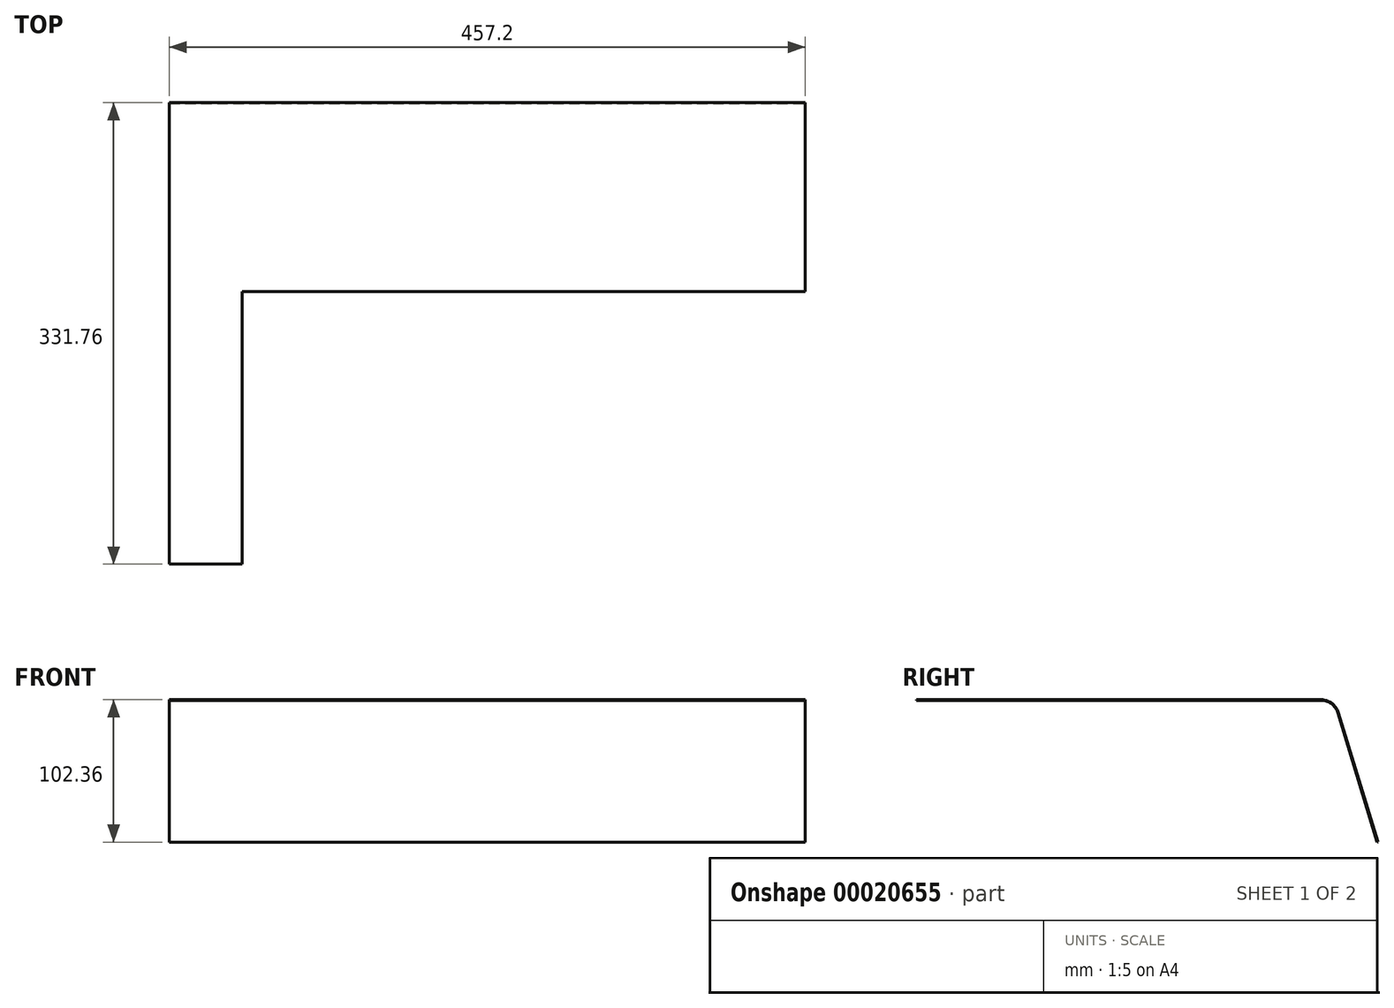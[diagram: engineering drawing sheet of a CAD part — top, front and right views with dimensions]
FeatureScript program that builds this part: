
annotation { "Feature Type Name" : "Feature", "Feature Type Description" : "" }
export const myFeature = defineFeature(function(context is Context, id is Id, definition is map)
    precondition{}
    {
        {
            var Q0;
            Q0=qCreatedBy(makeId("Right.planeOp"),FACE);
            var sketch = newSketch(context, id + "F0", { "sketchPlane" : qUnion([Q0])});
            skLineSegment(sketch, "E0", {"start": v(-259.13, 0) * mm, "end": v(31.98, 0) * mm});
            skLineSegment(sketch, "E1", {"start": v(44.12, -8.99) * mm, "end": v(72.63, -102.21) * mm});
            skPoint(sketch, "E2.visualSharp", {"position": v(41.38, 0) * mm});
            skArc(sketch, "E2.filletArc", {"start": v(44.12, -8.99) * mm, "mid": v(39.53, -2.5) * mm, "end": v(31.98, 0) * mm});
            skLineSegment(sketch, "E3.0", {"start": v(43.65, -9.13) * mm, "end": v(72.15, -102.36) * mm});
            skArc(sketch, "E3.1", {"start": v(43.65, -9.13) * mm, "mid": v(39.24, -2.9) * mm, "end": v(31.98, -0.5) * mm});
            skLineSegment(sketch, "E3.2", {"start": v(-259.13, -0.5) * mm, "end": v(31.98, -0.5) * mm});
            skLineSegment(sketch, "E4", {"start": v(-259.13, -0.5) * mm, "end": v(-259.13, 0) * mm});
            skLineSegment(sketch, "E5", {"start": v(72.15, -102.36) * mm, "end": v(72.63, -102.21) * mm});
            skSolve(sketch);
        }
        {
            var Q0;
            Q0=makeQuery(id+"F0.imprint","IMPRINT",FACE,{"disambiguationData":[TD([[makeQuery(id+"F0.imprint","IMPRINT",EDGE,{"derivedFrom":sQuery(id+"F0.wireOp",EDGE,"E0")}),-1.0]])]});
            extrude(context, id + "F1", {"entities" : qUnion([Q0]), "oppositeDirection" : true, "depth" : 457.2 * mm, "symmetric" : true});
        }
        {
            var Q0;
            Q0=qCreatedBy(makeId("Top.planeOp"),FACE);
            var sketch = newSketch(context, id + "F2", { "sketchPlane" : qUnion([Q0])});
            skCircle(sketch, "E6", {"center": v(-27.64, -26.13) * mm, "radius": 1.25 * mm});
            skCircle(sketch, "E7.0.1.0", {"center": v(-27.64, 26.13) * mm, "radius": 1.25 * mm});
            skCircle(sketch, "E7.1.0.0", {"center": v(27.64, -26.13) * mm, "radius": 1.25 * mm});
            skCircle(sketch, "E7.1.1.0", {"center": v(27.64, 26.13) * mm, "radius": 1.25 * mm});
            skSolve(sketch);
        }
        {
            var Q0;
            Q0=makeQuery(id+"F2.imprint","IMPRINT",FACE,{"disambiguationData":[TD([[makeQuery(id+"F2.imprint","IMPRINT",EDGE,{"derivedFrom":sQuery(id+"F2.wireOp",EDGE,"E7.0.1.0")}),1.0]])]});
            var Q1;
            Q1=makeQuery(id+"F2.imprint","IMPRINT",FACE,{"disambiguationData":[TD([[makeQuery(id+"F2.imprint","IMPRINT",EDGE,{"derivedFrom":sQuery(id+"F2.wireOp",EDGE,"E7.1.1.0")}),1.0]])]});
            var Q2;
            Q2=makeQuery(id+"F2.imprint","IMPRINT",FACE,{"disambiguationData":[TD([[makeQuery(id+"F2.imprint","IMPRINT",EDGE,{"derivedFrom":sQuery(id+"F2.wireOp",EDGE,"E6")}),1.0]])]});
            var Q3;
            Q3=makeQuery(id+"F2.imprint","IMPRINT",FACE,{"disambiguationData":[TD([[makeQuery(id+"F2.imprint","IMPRINT",EDGE,{"derivedFrom":sQuery(id+"F2.wireOp",EDGE,"E7.1.0.0")}),1.0]])]});
            var Q4;
            Q4=sQuery(id+"F2.wireOp",EDGE,"E6");
            var Q5;
            Q5=sQuery(id+"F2.wireOp",EDGE,"E7.1.0.0");
            var Q6;
            Q6=sQuery(id+"F2.wireOp",EDGE,"E7.1.1.0");
            var Q7;
            Q7=sQuery(id+"F2.wireOp",EDGE,"E7.0.1.0");
            extrude(context, id + "F3", {"entities" : qUnion([Q0, Q1, Q2, Q3]), "operationType" : NewBodyOperationType.REMOVE, "surfaceEntities" : qUnion([Q4, Q5, Q6, Q7]), "depth" : 10 * mm});
        }
        {
            var Q0;
            Q0=makeQuery(id+"F1.opExtrude","SWEPT_FACE",FACE,{"disambiguationData":[OSD([sQuery(id+"F0.wireOp",EDGE,"E0")])]});
            var sketch = newSketch(context, id + "F4", { "sketchPlane" : qUnion([Q0])});
            skLineSegment(sketch, "E8.bottom", {"start": v(-176.35, -63.02) * mm, "end": v(277.54, -63.02) * mm});
            skLineSegment(sketch, "E8.top", {"start": v(-176.35, -278.76) * mm, "end": v(277.54, -278.76) * mm});
            skLineSegment(sketch, "E8.left", {"start": v(-176.35, -63.02) * mm, "end": v(-176.35, -278.76) * mm});
            skLineSegment(sketch, "E8.right", {"start": v(277.54, -63.02) * mm, "end": v(277.54, -278.76) * mm});
            skSolve(sketch);
        }
        {
            var Q0;
            {var subQ2=sQuery(id+"F4.wireOp",EDGE,"E8.bottom");var subQ6=sQuery(id+"F4.wireOp",EDGE,"E8.left");var subQ8=makeQuery(id+"F4.imprint","INTERSECT",VERTEX,{"derivedFrom":[subQ2,subQ6]});Q0=makeQuery(id+"F4.imprint","IMPRINT",FACE,{"disambiguationData":[TD([[makeQuery(id+"F4.imprint","IMPRINT",EDGE,{"disambiguationData":[TD([[subQ8,-1.0]])],"derivedFrom":subQ2}),-1.0]])]});}
            var Q1;
            Q1=makeQuery(id+"F1.opExtrude","SWEPT_FACE",FACE,{"disambiguationData":[OSD([sQuery(id+"F0.wireOp",EDGE,"E3.2")])]});
            extrude(context, id + "F5", {"entities" : qUnion([Q0]), "operationType" : NewBodyOperationType.REMOVE, "oppositeDirection" : true, "endBoundEntity" : qUnion([Q1]), "depth" : 25 * mm});
        }
    });
